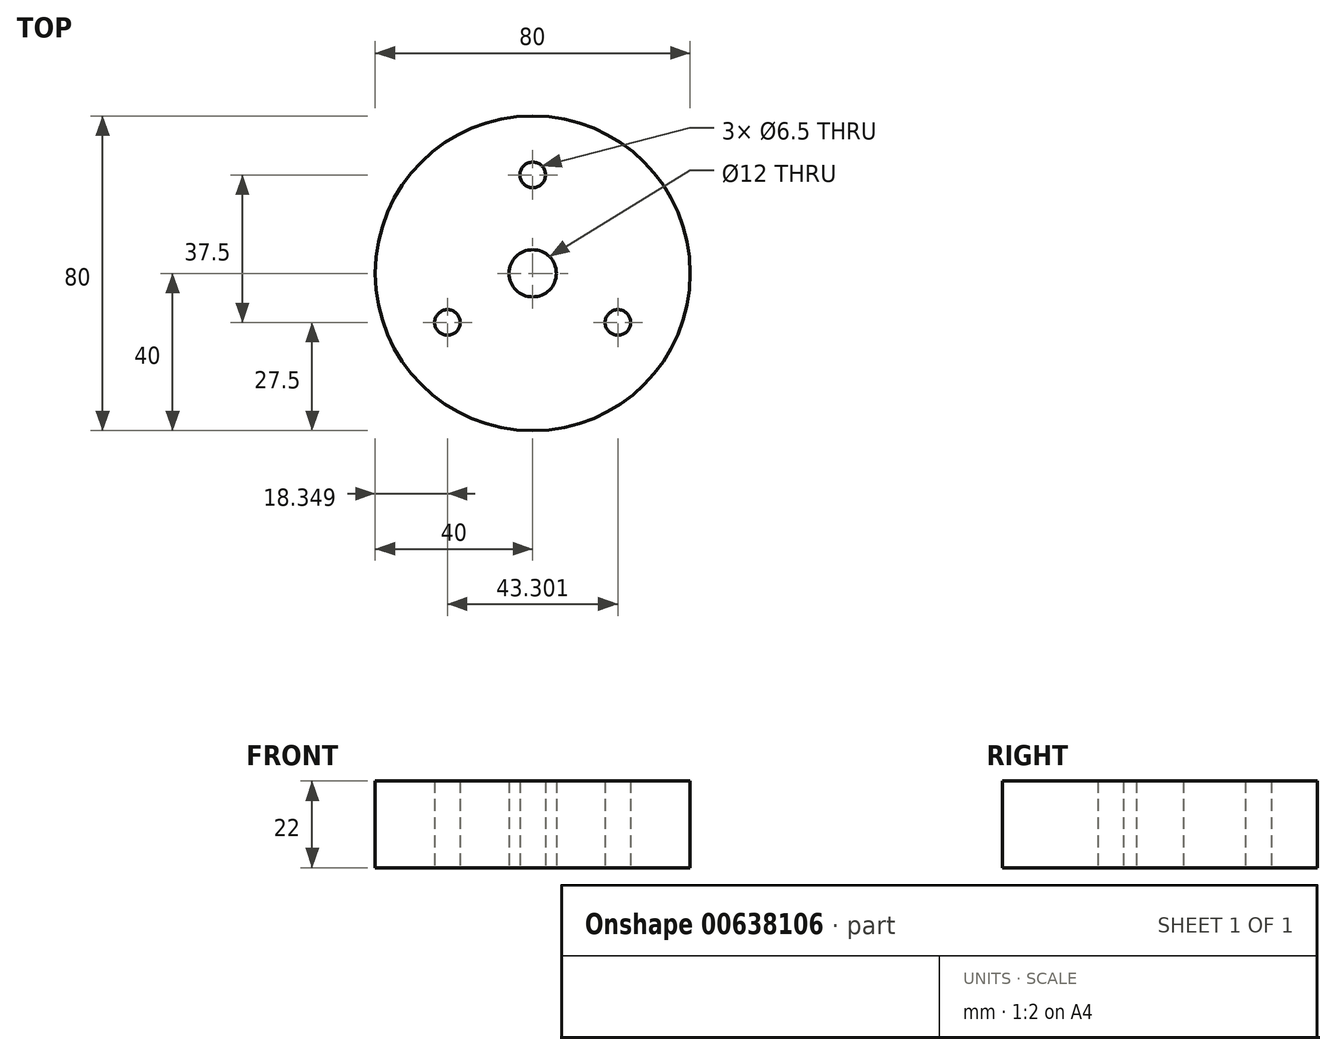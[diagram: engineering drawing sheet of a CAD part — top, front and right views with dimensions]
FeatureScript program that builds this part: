
annotation { "Feature Type Name" : "Feature", "Feature Type Description" : "" }
export const myFeature = defineFeature(function(context is Context, id is Id, definition is map)
    precondition{}
    {
        {
            var Q0;
            Q0=qCreatedBy(makeId("Top.planeOp"),FACE);
            var sketch = newSketch(context, id + "F0", { "sketchPlane" : qUnion([Q0])});
            skCircle(sketch, "E0", {"center": v(0, 0) * mm, "radius": 40 * mm});
            skLineSegment(sketch, "E1", {"start": v(0, 0) * mm, "end": v(0, 25) * mm, "construction": true});
            skLineSegment(sketch, "E2", {"start": v(0, 0) * mm, "end": v(-21.65, -12.5) * mm, "construction": true});
            skLineSegment(sketch, "E3", {"start": v(0, 0) * mm, "end": v(21.65, -12.5) * mm, "construction": true});
            skCircle(sketch, "E4", {"center": v(0, 0) * mm, "radius": 25 * mm, "construction": true});
            skCircle(sketch, "E5", {"center": v(-21.65, -12.5) * mm, "radius": 3.25 * mm});
            skCircle(sketch, "E6", {"center": v(0, 25) * mm, "radius": 3.25 * mm});
            skCircle(sketch, "E7", {"center": v(21.65, -12.5) * mm, "radius": 3.25 * mm});
            skCircle(sketch, "E8", {"center": v(0, 0) * mm, "radius": 6 * mm});
            skSolve(sketch);
        }
        {
            var Q0;
            Q0=makeQuery(id+"F0.imprint","IMPRINT",FACE,{"disambiguationData":[TD([[makeQuery(id+"F0.imprint","IMPRINT",EDGE,{"derivedFrom":sQuery(id+"F0.wireOp",EDGE,"E0")}),1.0]])]});
            extrude(context, id + "F1", {"entities" : qUnion([Q0]), "depth" : 22 * mm, "offsetDistance" : 25 * mm});
        }
    });
